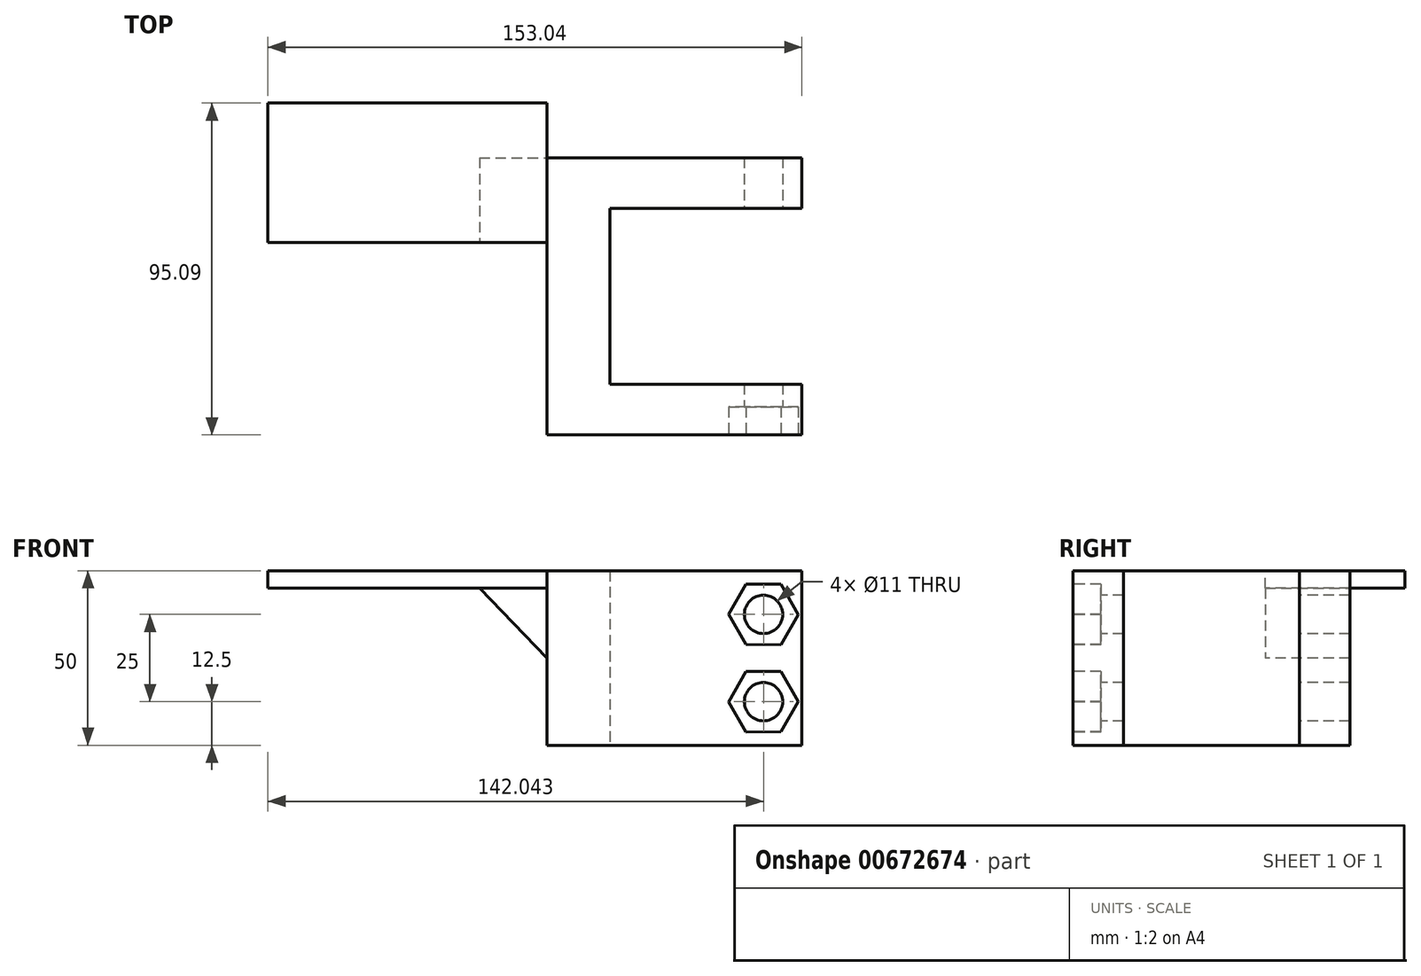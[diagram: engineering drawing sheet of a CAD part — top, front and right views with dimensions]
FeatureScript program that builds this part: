
annotation { "Feature Type Name" : "Feature", "Feature Type Description" : "" }
export const myFeature = defineFeature(function(context is Context, id is Id, definition is map)
    precondition{}
    {
        {
            var Q0;
            Q0=qCreatedBy(makeId("Top.planeOp"),FACE);
            var sketch = newSketch(context, id + "F0", { "sketchPlane" : qUnion([Q0])});
            skLineSegment(sketch, "E0.bottom", {"start": v(9.02, 39.7) * mm, "end": v(-9.02, 39.7) * mm});
            skLineSegment(sketch, "E0.top", {"start": v(9.02, -39.7) * mm, "end": v(-9.02, -39.7) * mm});
            skLineSegment(sketch, "E0.left", {"start": v(9.02, 39.7) * mm, "end": v(9.02, -39.7) * mm});
            skLineSegment(sketch, "E0.right", {"start": v(-9.02, 39.7) * mm, "end": v(-9.02, -39.7) * mm});
            skPoint(sketch, "E0.middle", {"position": v(0, 0) * mm});
            skLineSegment(sketch, "E1.bottom", {"start": v(9.02, 39.7) * mm, "end": v(64.02, 39.7) * mm});
            skLineSegment(sketch, "E1.top", {"start": v(9.02, 25.2) * mm, "end": v(64.02, 25.2) * mm});
            skLineSegment(sketch, "E1.left", {"start": v(9.02, 39.7) * mm, "end": v(9.02, 25.2) * mm});
            skLineSegment(sketch, "E1.right", {"start": v(64.02, 39.7) * mm, "end": v(64.02, 25.2) * mm});
            skLineSegment(sketch, "E2.MirrorCS", {"start": v(9.02, -25.2) * mm, "end": v(64.02, -25.2) * mm});
            skLineSegment(sketch, "E3.MirrorCS", {"start": v(9.02, -39.7) * mm, "end": v(9.02, -25.2) * mm});
            skLineSegment(sketch, "E4.MirrorCS", {"start": v(9.02, -39.7) * mm, "end": v(64.02, -39.7) * mm});
            skLineSegment(sketch, "E5.MirrorCS", {"start": v(64.02, -39.7) * mm, "end": v(64.02, -25.2) * mm});
            skLineSegment(sketch, "E6", {"start": v(9.02, -25.2) * mm, "end": v(9.02, 25.2) * mm});
            skSolve(sketch);
        }
        {
            var Q0;
            Q0=qSketchRegion(id+"F0",true);
            extrude(context, id + "F1", {"entities" : qUnion([Q0]), "depth" : 50 * mm, "offsetDistance" : 25 * mm});
        }
        {
            var Q0;
            Q0=makeQuery(id+"F1.opExtrude","SWEPT_FACE",FACE,{"disambiguationData":[OSD([sQuery(id+"F0.wireOp",EDGE,"E0.top"),sQuery(id+"F0.wireOp",EDGE,"E4.MirrorCS")])]});
            var sketch = newSketch(context, id + "F2", { "sketchPlane" : qUnion([Q0])});
            skLineSegment(sketch, "E7", {"start": v(64.02, 25) * mm, "end": v(-9.02, 25) * mm});
            skLineSegment(sketch, "E8", {"start": v(64.02, 25) * mm, "end": v(42.02, 25) * mm});
            skLineSegment(sketch, "E9", {"start": v(53.02, 25) * mm, "end": v(53.02, 50) * mm});
            skLineSegment(sketch, "E10", {"start": v(53.02, 25) * mm, "end": v(53.02, 0) * mm});
            skPoint(sketch, "E11", {"position": v(53.02, 37.5) * mm});
            skPoint(sketch, "E12", {"position": v(53.02, 12.5) * mm});
            skCircle(sketch, "E13.cCircle", {"center": v(53.02, 37.5) * mm, "radius": 8.65 * mm, "construction": true});
            skLineSegment(sketch, "E13.0", {"start": v(58.04, 46.13) * mm, "end": v(63.01, 37.47) * mm});
            skLineSegment(sketch, "E13.1", {"start": v(63.01, 37.47) * mm, "end": v(57.99, 28.83) * mm});
            skLineSegment(sketch, "E13.2", {"start": v(57.99, 28.83) * mm, "end": v(48, 28.87) * mm});
            skLineSegment(sketch, "E13.3", {"start": v(48, 28.87) * mm, "end": v(43.03, 37.53) * mm});
            skLineSegment(sketch, "E13.4", {"start": v(43.03, 37.53) * mm, "end": v(48.06, 46.17) * mm});
            skLineSegment(sketch, "E13.5", {"start": v(48.06, 46.17) * mm, "end": v(58.04, 46.13) * mm});
            skPoint(sketch, "E13.0.midPoint", {"position": v(60.53, 41.8) * mm});
            skCircle(sketch, "E14.MirrorC", {"center": v(53.02, 12.5) * mm, "radius": 8.65 * mm, "construction": true});
            skLineSegment(sketch, "E15.MirrorCS", {"start": v(58.04, 3.87) * mm, "end": v(63.01, 12.53) * mm});
            skLineSegment(sketch, "E16.MirrorCS", {"start": v(63.01, 12.53) * mm, "end": v(57.99, 21.17) * mm});
            skLineSegment(sketch, "E17.MirrorCS", {"start": v(57.99, 21.17) * mm, "end": v(48, 21.13) * mm});
            skLineSegment(sketch, "E18.MirrorCS", {"start": v(48, 21.13) * mm, "end": v(43.03, 12.47) * mm});
            skLineSegment(sketch, "E19.MirrorCS", {"start": v(43.03, 12.47) * mm, "end": v(48.06, 3.83) * mm});
            skLineSegment(sketch, "E20.MirrorCS", {"start": v(48.06, 3.83) * mm, "end": v(58.04, 3.87) * mm});
            skLineSegment(sketch, "E21", {"start": v(48, 28.87) * mm, "end": v(48.06, 46.17) * mm, "construction": true});
            skSolve(sketch);
        }
        {
            var Q0;
            Q0=sQuery(id+"F2.wireOp",VERTEX,"E11");
            var Q1;
            Q1=sQuery(id+"F2.wireOp",VERTEX,"E12");
            var Q2;
            Q2=makeQuery(id+"F1.opExtrude","SWEPT_BODY",BODY,{"disambiguationData":[OSD([sQuery(id+"F0.wireOp",EDGE,"E0.bottom"),sQuery(id+"F0.wireOp",EDGE,"E0.top"),sQuery(id+"F0.wireOp",EDGE,"E0.right"),sQuery(id+"F0.wireOp",EDGE,"E1.bottom"),sQuery(id+"F0.wireOp",EDGE,"E1.top"),sQuery(id+"F0.wireOp",EDGE,"E1.right"),sQuery(id+"F0.wireOp",EDGE,"E2.MirrorCS"),sQuery(id+"F0.wireOp",EDGE,"E4.MirrorCS"),sQuery(id+"F0.wireOp",EDGE,"E5.MirrorCS"),sQuery(id+"F0.wireOp",EDGE,"E6")])]});
            hole(context, id + "F3", {"style" : HoleStyle.SIMPLE, "endStyle" : HoleEndStyle.THROUGH, "holeDiameter" : 11 * mm, "majorDiameter" : 5 * mm, "isTappedThrough" : true, "tappedDepth" : 12 * mm, "tapClearance" : 3, "locations" : qUnion([Q0, Q1]), "scope" : qUnion([Q2])});
        }
        {
            var Q0;
            Q0=makeQuery(id+"F1.opExtrude","CAP_FACE",FACE,{"disambiguationData":[OSD([sQuery(id+"F0.wireOp",EDGE,"E0.bottom"),sQuery(id+"F0.wireOp",EDGE,"E0.top"),sQuery(id+"F0.wireOp",EDGE,"E0.right"),sQuery(id+"F0.wireOp",EDGE,"E1.bottom"),sQuery(id+"F0.wireOp",EDGE,"E1.top"),sQuery(id+"F0.wireOp",EDGE,"E1.right"),sQuery(id+"F0.wireOp",EDGE,"E2.MirrorCS"),sQuery(id+"F0.wireOp",EDGE,"E4.MirrorCS"),sQuery(id+"F0.wireOp",EDGE,"E5.MirrorCS"),sQuery(id+"F0.wireOp",EDGE,"E6")])],"isStart":false});
            var sketch = newSketch(context, id + "F4", { "sketchPlane" : qUnion([Q0])});
            skLineSegment(sketch, "E22.bottom", {"start": v(-9.02, 15.39) * mm, "end": v(-89.02, 15.39) * mm});
            skLineSegment(sketch, "E22.top", {"start": v(-9.02, 55.39) * mm, "end": v(-89.02, 55.39) * mm});
            skLineSegment(sketch, "E22.left", {"start": v(-9.02, 15.39) * mm, "end": v(-9.02, 55.39) * mm});
            skLineSegment(sketch, "E22.right", {"start": v(-89.02, 15.39) * mm, "end": v(-89.02, 55.39) * mm});
            skLineSegment(sketch, "E23.MirrorCS", {"start": v(-9.02, -15.39) * mm, "end": v(-89.02, -15.39) * mm});
            skLineSegment(sketch, "E24.MirrorCS", {"start": v(-9.02, -55.39) * mm, "end": v(-89.02, -55.39) * mm});
            skLineSegment(sketch, "E25.MirrorCS", {"start": v(-9.02, -15.39) * mm, "end": v(-9.02, -55.39) * mm});
            skLineSegment(sketch, "E26.MirrorCS", {"start": v(-89.02, -15.39) * mm, "end": v(-89.02, -55.39) * mm});
            skSolve(sketch);
        }
        {
            var Q0;
            {var subQ3=sQuery(id+"F4.wireOp",EDGE,"E22.bottom");Q0=makeQuery(id+"F4.imprint","IMPRINT",FACE,{"disambiguationData":[TD([[makeQuery(id+"F4.imprint","IMPRINT",EDGE,{"derivedFrom":subQ3}),-1.0]])]});}
            extrude(context, id + "F5", {"entities" : qUnion([Q0]), "oppositeDirection" : true, "depth" : 5 * mm, "offsetDistance" : 25 * mm});
        }
        {
            var Q0;
            Q0=makeQuery(id+"F1.opExtrude","SWEPT_FACE",FACE,{"disambiguationData":[OSD([sQuery(id+"F0.wireOp",EDGE,"E0.top"),sQuery(id+"F0.wireOp",EDGE,"E4.MirrorCS")])]});
            var sketch = newSketch(context, id + "F6", { "sketchPlane" : qUnion([Q0])});
            skLineSegment(sketch, "E27.0.0", {"start": v(-9.02, 50) * mm, "end": v(-89.02, 50) * mm});
            skLineSegment(sketch, "E27.0.1", {"start": v(-89.02, 50) * mm, "end": v(-89.02, 45) * mm});
            skLineSegment(sketch, "E27.0.2", {"start": v(-89.02, 45) * mm, "end": v(-9.02, 45) * mm});
            skLineSegment(sketch, "E27.0.3", {"start": v(-9.02, 45) * mm, "end": v(-9.02, 50) * mm});
            skLineSegment(sketch, "E28", {"start": v(-28.38, 45) * mm, "end": v(-9.02, 25) * mm});
            skSolve(sketch);
        }
        {
            var Q0;
            {var subQ3=sQuery(id+"F6.wireOp",EDGE,"E28");Q0=makeQuery(id+"F6.imprint","IMPRINT",FACE,{"disambiguationData":[TD([[makeQuery(id+"F6.imprint","IMPRINT",EDGE,{"derivedFrom":subQ3}),1.0]])]});}
            var Q1;
            Q1=makeQuery(id+"F1.opExtrude","SWEPT_FACE",FACE,{"disambiguationData":[OSD([sQuery(id+"F0.wireOp",EDGE,"E0.bottom"),sQuery(id+"F0.wireOp",EDGE,"E1.bottom")])]});
            var Q2;
            Q2=makeQuery(id+"F5.opExtrude","SWEPT_FACE",FACE,{"disambiguationData":[OSD([sQuery(id+"F4.wireOp",EDGE,"E22.bottom")])]});
            extrude(context, id + "F7", {"entities" : qUnion([Q0]), "endBound" : BoundingType.UP_TO_SURFACE, "oppositeDirection" : true, "depth" : 25 * mm, "endBoundEntityFace" : qUnion([Q1]), "offsetDistance" : 25 * mm, "hasSecondDirection" : true, "secondDirectionBound" : SecondDirectionBoundingType.UP_TO_SURFACE, "secondDirectionOppositeDirection" : true, "secondDirectionDepth" : 25 * mm, "secondDirectionBoundEntityFace" : qUnion([Q2])});
        }
        {
            var Q0;
            Q0=qSketchRegion(id+"F2",true);
            extrude(context, id + "F8", {"entities" : qUnion([Q0]), "operationType" : NewBodyOperationType.REMOVE, "oppositeDirection" : true, "depth" : 8 * mm, "offsetDistance" : 25 * mm});
        }
    });
